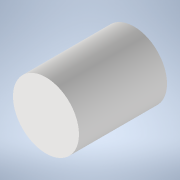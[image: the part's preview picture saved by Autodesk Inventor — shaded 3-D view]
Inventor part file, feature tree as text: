
AUTODESK INVENTOR PART (.ipt)
format: ipt  version: 2022 (Build 260153000, 153)  size: 91,136 bytes
history: native  units: mm
features: extrude x1, sketch x1
ambient origin geometry x8: Origin, YZ Plane, XZ Plane, XY Plane, X Axis, Y Axis, Z Axis, Center Point
bodies: Volumenkörper1 (feature_tree)
feature tree (2):
  extrude  "Extrusion1"  Depth=8.0mm TaperAngle=0.0deg
  sketch  "Skizze1"  dims[d0=6.0mm d1=8.0mm d2=0.0mm]
